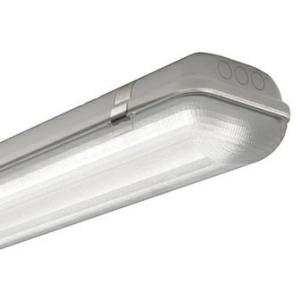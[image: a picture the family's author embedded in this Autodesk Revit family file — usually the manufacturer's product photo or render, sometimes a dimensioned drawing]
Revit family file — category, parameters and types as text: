
# Revit family: 3f_filippi_-_3f_linda_3f_filippi_-_58572_-_3f_linda_led_2x12w_l660
name_source: partatom
category: Lighting Fixtures
units: mm (PartAtom-declared; Revit-internal decimal feet)

## family parameters
Cut with Voids When Loaded = No
Host = Face
Light Source = No
Part Type = Normal
Room Calculation Point = No
Round Connector Dimension = Use Diameter
Shared = No

## types (1)
- 3F Filippi - 3F Linda (1 x LED, 3955 lm, 28 W, 4000 K)
    Apparent Load = 28 VA
    Approval mark = CE
    CIE Flux Codes = 46 76 93 97 100
    Color Rendering = 80
    Color Temperature = 4000 K
    Control Gear = Electronic ballast
    Default Elevation = 1800 mm
    Description = ILLUMINOTECHNICAL
Luminous efficiency 100% (DLOR 97%, ULOR 3%).
Initial luminous flux of the luminaire 3955 lm.
Controlled symmetric distribution.
Installation Interdistance Transv.D = 1.52 x hu - Long.D = 1.17 x hu.
Tabular UGR (CIE 117 - 4H-8H; S=0.25H; 70/50/20): RUG 24.2 - 23.1.
Beam angle: 94° - 78°.
Luminous efficacy 141 lm/W.
Lifetime (L93/B10): 30000 h. (tq+25°C)
Lifetime (L90/B10): 50000 h. (tq+25°C)
Lifetime (L85/B10): 80000 h. (tq+25°C)
Lifetime (L80/B10): 100000 h. (tq+25°C)
Lifetime (L85/B10): 50000 h. (tq+35°C)
Sudden decreased luminous flux after 50000 hours: 0% (C0).
Photobiological safety in compliance with IEC/TR 62778: RG0 risk exempt, (IEC 62471).
In compliance with IEC/EN 62722-2-1 - IEC/EN 62717 standards.

SOURCE
2 linear LED modules 12W/840.
Energy efficiency class (UE 2019/2020 - UE 2019/2015): D.
CIE 13.3 Colour rendering index: CRI >80 (R9 <50%).
IES TM-30 Fidelity Index: Rf = 84 Rg = 95.
CCT nominal colour temperature 4000 K.
Colour initial tolerance (MacAdam): SDCM 3.

MECHANICAL
Self-extinguishing V2 polycarbonate housing, injection moulded, RAL 7035 grey.
Ecologic anti-aging injected sealing gasket.
Diffuser in self-extinguishing V2 polycarbonate, photo-engraved interior, UV stabilised, injection moulded with smooth outer surface, tamper-proof opening.
Gear-holder reflector in hot-dip galvanised steel, painted with white polyester base.
Snug fit safety snap-lock clips for diffuser mounting in stainless steel, screwdriver opening.
Fixing brackets in stainless steel.
Possibility for technicians to access the interior of the luminaire.
Luminaire with limited surface temperature. - D - (EN 60598-2-24)
Dimensions: 660x160 mm, height 100 mm. Weight 1.725 kg.
IP66 protection degree.
Mechanical strength to impacts IK10 (20 joule).
Glow-wire test resistance 850°C.

ELECTRICAL
Halogen Free electronic wiring 230V-50/60Hz, power factor 0.90, THD <25%, constant output current, SELV, class I, 1 driver.
Power of the luminaire 28 W.
ENEC - CE.
SAFE FLICKER: PstLM=<1 and SVM=<0.4 (IEC TR 61547-1 and IEC TR 63158), to ensure a more comfortable and safe light.
Luminaire compliant with EN 60598-2-22 for power supply from a centralised emergency system CPSS (Central Power Supply System), not incorporated in the luminaire - high risk areas excluded. The default power and flux are 100% in AC and 100% in DC.
Ambient temperature from -20°C to +35°C.
Temperature class T6 max 85°C.
Relative humidity UR: <85%.

INSTALLATION
Ceiling / Suspended / Wall.
All accessories dedicated to this product are available on the Catalog and on our website www.3F-Filippi.com.

APPLICATIONS
Suitable product for food production plants (HACCP), IFS (Food Version 6), BRC (GSFS Food Version 7).
Dry, dusty indoor environments, subject to occasional water splashes.
Virtually shatterproof polycarbonate compatibly with the fumes / atmospheres that compromise the elasticity of plastic materials.
Not suitable for installation on surfaces subject to important vibrations, exposed to weather conditions, on ropes or poles.
Suitable for illumination of public car parks and parking grounds referred to DIN 67528:2018-04.

WARNING
Fixture not suitable for cold stores with an ambient temperature <0°C and/or relative humidity >85%.
Luminaire designed for disposal/recycling at end-of-life.
Replaceable (LED only) light source by a professional. Replaceable control gear by a professional.
    Height = 100 mm  [stored 0.328084 ft]
    Lamp = 1 x LED
    Lamp Light Flux = 3955 lm
    Lamp Power = 28 W
    Lamp count = 1
    Length = 660 mm
    Lifetime = 50000 h
    Luminous efficacy = 141 lm/W
    Manufacturer = 3F Filippi
    ModVariant = No
    Model = 3F Filippi - 58572 - 3F Linda LED 2x12W L660
    Mounting Place = Ceiling
    Mounting Type = Pendant
    Number of Poles = 1
    OnlyDefault = Yes
    Power Factor = 1
    Product Name = 3F Filippi - 3F Linda
    Product group = pendant luminaire
    ProductGroupID = 9
    Protection Class = Protection class I
    Protection Degree = IP 66
    RLX_Detail_Level = 1
    RLX_Emergency_Light_Flux = 0 lm
    RLX_Emergency_Type = 0
    RLX_Emergency_Type_DB = No
    RlxData = <blob elided: 71709 chars, md5=afc2249a>
    Socket = socket
    Standby Power = 0 W
    System Light Flux = 3955 lm
    System Power = 28 W
    Type Comments = Product without accessories
    Type Image = 3ffilippi_58572.jpg
    URL = http://relux.com
    VarID = ---
    Voltage = 0 V
    Weight = 0.00 kg
    Width = 160 mm

note: [stored X ft] marks values corroborated as IEEE doubles in the binary element streams (Revit-internal decimal feet)

## geometry (parser evidence)
native form markers: Blend x4, Sweep x10
no freeform markers — native parametric forms only
